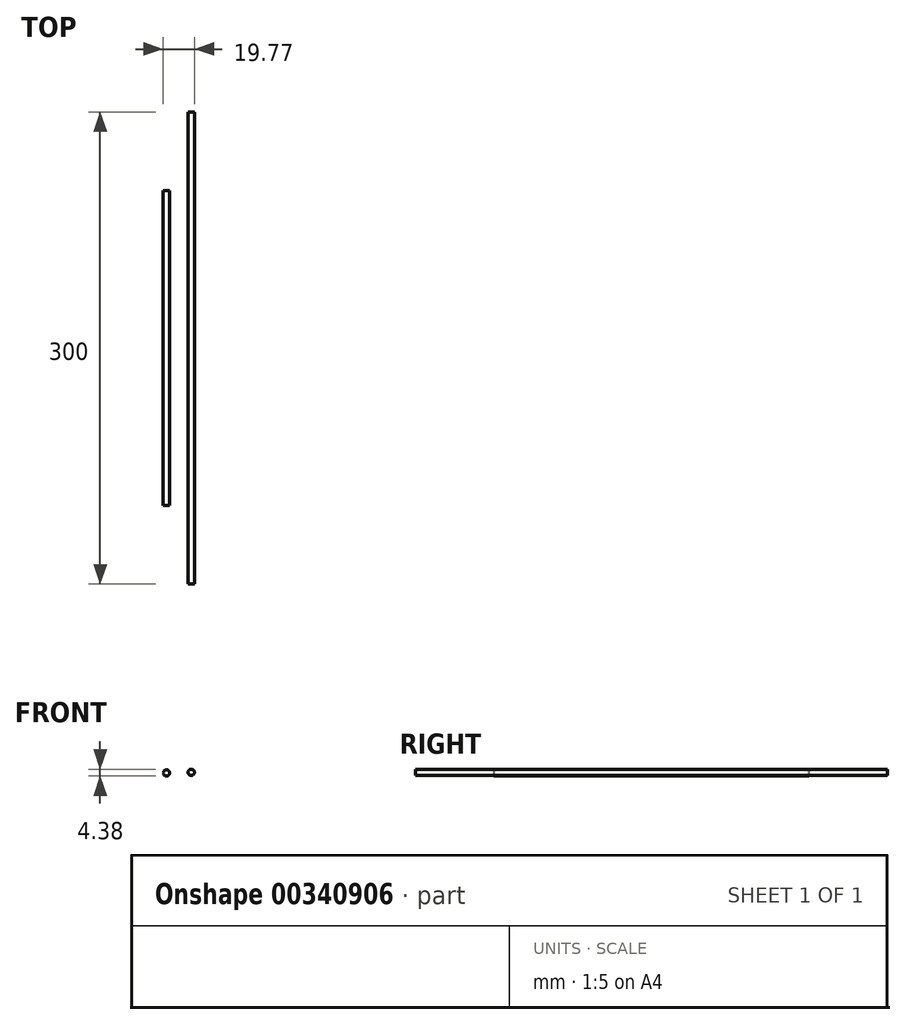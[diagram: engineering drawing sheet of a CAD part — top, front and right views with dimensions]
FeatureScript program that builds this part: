
annotation { "Feature Type Name" : "Feature", "Feature Type Description" : "" }
export const myFeature = defineFeature(function(context is Context, id is Id, definition is map)
    precondition{}
    {
        {
            var Q0;
            Q0=qCreatedBy(makeId("Front.planeOp"),FACE);
            var sketch = newSketch(context, id + "F0", { "sketchPlane" : qUnion([Q0])});
            skCircle(sketch, "E0", {"center": v(-36.1, 19.38) * mm, "radius": 2 * mm});
            skCircle(sketch, "E1", {"center": v(-20.33, 19.76) * mm, "radius": 2 * mm});
            skSolve(sketch);
        }
        {
            var Q0;
            Q0=makeQuery(id+"F0.imprint","IMPRINT",FACE,{"disambiguationData":[TD([[makeQuery(id+"F0.imprint","IMPRINT",EDGE,{"derivedFrom":sQuery(id+"F0.wireOp",EDGE,"E0")}),1.0]])]});
            extrude(context, id + "F1", {"entities" : qUnion([Q0]), "endBound" : BoundingType.SYMMETRIC, "depth" : 200 * mm, "offsetDistance" : 25 * mm});
        }
        {
            var Q0;
            Q0=makeQuery(id+"F0.imprint","IMPRINT",FACE,{"disambiguationData":[TD([[makeQuery(id+"F0.imprint","IMPRINT",EDGE,{"derivedFrom":sQuery(id+"F0.wireOp",EDGE,"E1")}),1.0]])]});
            extrude(context, id + "F2", {"entities" : qUnion([Q0]), "endBound" : BoundingType.SYMMETRIC, "depth" : 300 * mm, "offsetDistance" : 25 * mm});
        }
    });
